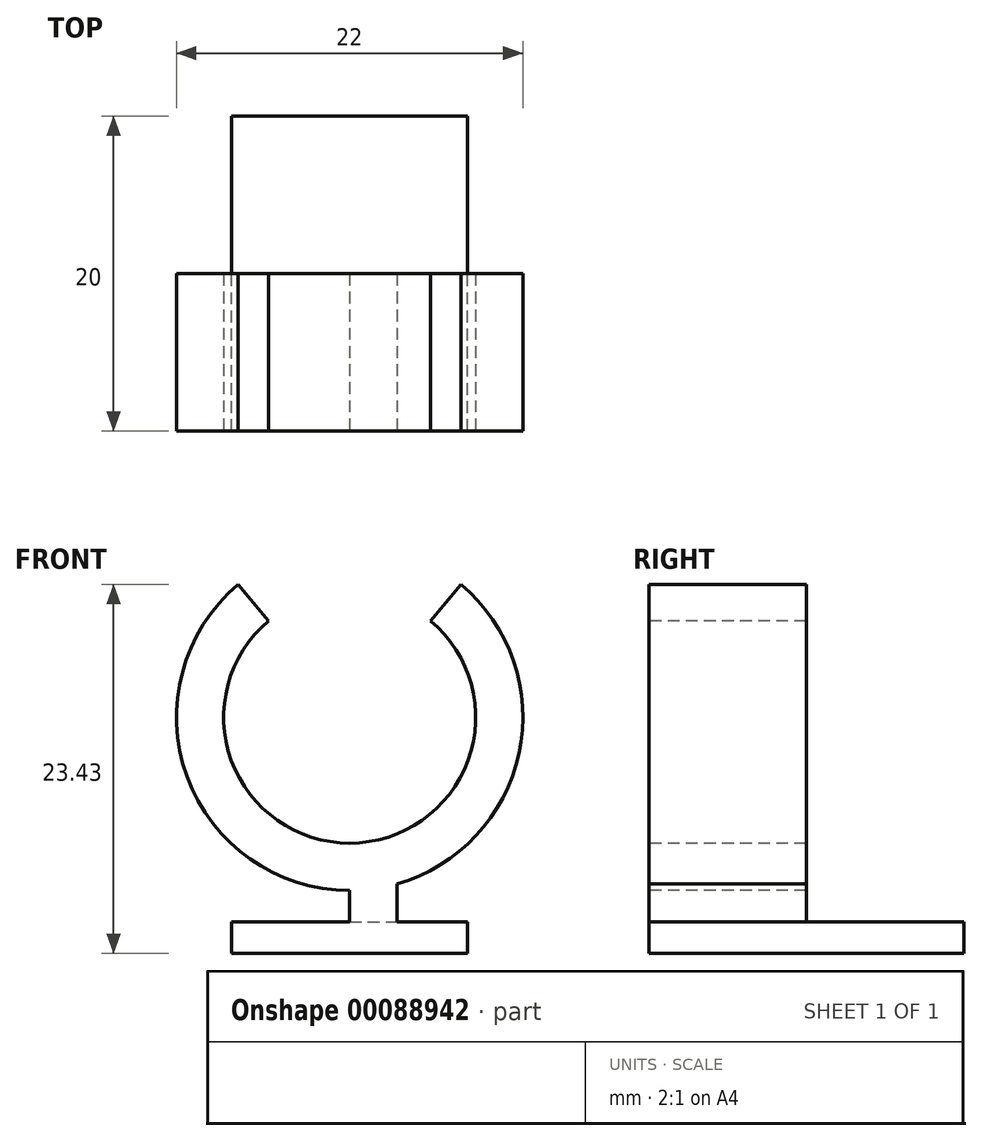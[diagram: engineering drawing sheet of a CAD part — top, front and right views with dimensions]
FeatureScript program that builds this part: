
annotation { "Feature Type Name" : "Feature", "Feature Type Description" : "" }
export const myFeature = defineFeature(function(context is Context, id is Id, definition is map)
    precondition{}
    {
        {
            var Q0;
            Q0=qCreatedBy(makeId("Top.planeOp"),FACE);
            var sketch = newSketch(context, id + "F0", { "sketchPlane" : qUnion([Q0])});
            skLineSegment(sketch, "E0.bottom", {"start": v(0, 0) * mm, "end": v(14.98, 0) * mm});
            skLineSegment(sketch, "E0.top", {"start": v(0, 20) * mm, "end": v(14.98, 20) * mm});
            skLineSegment(sketch, "E0.left", {"start": v(0, 0) * mm, "end": v(0, 20) * mm});
            skLineSegment(sketch, "E0.right", {"start": v(14.98, 0) * mm, "end": v(14.98, 20) * mm});
            skSolve(sketch);
        }
        {
            var Q0;
            Q0=makeQuery(id+"F0.imprint","IMPRINT",FACE,{"disambiguationData":[TD([[makeQuery(id+"F0.imprint","IMPRINT",EDGE,{"derivedFrom":sQuery(id+"F0.wireOp",EDGE,"E0.bottom")}),1.0]])]});
            extrude(context, id + "F1", {"entities" : qUnion([Q0]), "oppositeDirection" : true, "depth" : 2 * mm});
        }
        {
            var Q0;
            Q0=makeQuery(id+"F1.opExtrude","SWEPT_FACE",FACE,{"disambiguationData":[OSD([sQuery(id+"F0.wireOp",EDGE,"E0.bottom")])]});
            var sketch = newSketch(context, id + "F2", { "sketchPlane" : qUnion([Q0])});
            skLineSegment(sketch, "E1", {"start": v(0, 0) * mm, "end": v(7.49, 0) * mm});
            skLineSegment(sketch, "E2", {"start": v(7.49, 0) * mm, "end": v(4.49, 0) * mm});
            skLineSegment(sketch, "E3", {"start": v(4.49, 0) * mm, "end": v(4.49, 5) * mm});
            skLineSegment(sketch, "E4", {"start": v(4.49, 5) * mm, "end": v(10.49, 5) * mm});
            skLineSegment(sketch, "E5", {"start": v(10.49, 5) * mm, "end": v(10.49, 0) * mm});
            skLineSegment(sketch, "E6", {"start": v(7.49, 0) * mm, "end": v(7.49, 5) * mm});
            skLineSegment(sketch, "E7", {"start": v(7.49, 5) * mm, "end": v(7.49, 13) * mm});
            skCircle(sketch, "E8", {"center": v(7.49, 13) * mm, "radius": 8 * mm});
            skCircle(sketch, "E9", {"center": v(7.49, 13) * mm, "radius": 11 * mm});
            skLineSegment(sketch, "E10", {"start": v(7.49, 13) * mm, "end": v(-3.51, 13) * mm});
            skLineSegment(sketch, "E11", {"start": v(7.49, 13) * mm, "end": v(0.42, 21.43) * mm});
            skLineSegment(sketch, "E12", {"start": v(7.49, 13) * mm, "end": v(14.56, 21.43) * mm});
            skSolve(sketch);
        }
        {
            var Q0;
            {var subQ0=sQuery(id+"F2.wireOp",EDGE,"E5");var subQ1=makeQuery(id+"F1.opExtrude","CAP_EDGE",EDGE,{"disambiguationData":[OSD([sQuery(id+"F0.wireOp",EDGE,"E0.bottom")])],"isStart":true});var subQ2=makeQuery(id+"F2.imprint","INTERSECT",VERTEX,{"derivedFrom":[subQ1,subQ0]});Q0=makeQuery(id+"F2.imprint","IMPRINT",FACE,{"disambiguationData":[TD([[makeQuery(id+"F2.imprint","IMPRINT",EDGE,{"disambiguationData":[TD([[subQ2,1.0]])],"derivedFrom":subQ0}),-1.0]])]});}
            var Q1;
            {var subQ0=sQuery(id+"F2.wireOp",EDGE,"E2");Q1=makeQuery(id+"F2.imprint","IMPRINT",FACE,{"disambiguationData":[TD([[makeQuery(id+"F2.imprint","IMPRINT",EDGE,{"derivedFrom":subQ0}),1.0]])]});}
            var Q2;
            {var subQ0=sQuery(id+"F2.wireOp",EDGE,"E4");var subQ1=sQuery(id+"F2.wireOp",EDGE,"E3");var subQ2=makeQuery(id+"F2.imprint","INTERSECT",VERTEX,{"derivedFrom":[subQ1,subQ0]});Q2=makeQuery(id+"F2.imprint","IMPRINT",FACE,{"disambiguationData":[TD([[makeQuery(id+"F2.imprint","IMPRINT",EDGE,{"disambiguationData":[TD([[subQ2,1.0]])],"derivedFrom":subQ1}),-1.0]])]});}
            var Q3;
            {var subQ0=sQuery(id+"F2.wireOp",EDGE,"E5");var subQ1=sQuery(id+"F2.wireOp",EDGE,"E4");var subQ2=makeQuery(id+"F2.imprint","INTERSECT",VERTEX,{"derivedFrom":[subQ1,subQ0]});Q3=makeQuery(id+"F2.imprint","IMPRINT",FACE,{"disambiguationData":[TD([[makeQuery(id+"F2.imprint","IMPRINT",EDGE,{"disambiguationData":[TD([[subQ2,-1.0]])],"derivedFrom":subQ0}),-1.0]])]});}
            var Q4;
            {var subQ3=sQuery(id+"F2.wireOp",EDGE,"E5");var subQ6=sQuery(id+"F2.wireOp",EDGE,"E4");var subQ9=makeQuery(id+"F2.imprint","INTERSECT",VERTEX,{"derivedFrom":[subQ6,subQ3]});Q4=makeQuery(id+"F2.imprint","IMPRINT",FACE,{"disambiguationData":[TD([[makeQuery(id+"F2.imprint","IMPRINT",EDGE,{"disambiguationData":[TD([[subQ9,-1.0]])],"derivedFrom":subQ3}),1.0]])]});}
            var Q5;
            {var subQ3=sQuery(id+"F2.wireOp",EDGE,"E3");var subQ6=sQuery(id+"F2.wireOp",EDGE,"E4");var subQ9=makeQuery(id+"F2.imprint","INTERSECT",VERTEX,{"derivedFrom":[subQ3,subQ6]});Q5=makeQuery(id+"F2.imprint","IMPRINT",FACE,{"disambiguationData":[TD([[makeQuery(id+"F2.imprint","IMPRINT",EDGE,{"disambiguationData":[TD([[subQ9,1.0]])],"derivedFrom":subQ3}),1.0]])]});}
            var Q6;
            {var subQ0=sQuery(id+"F2.wireOp",EDGE,"E11");var subQ1=sQuery(id+"F2.wireOp",EDGE,"E8");var subQ2=makeQuery(id+"F2.imprint","INTERSECT",VERTEX,{"derivedFrom":[subQ1,subQ0]});Q6=makeQuery(id+"F2.imprint","IMPRINT",FACE,{"disambiguationData":[TD([[makeQuery(id+"F2.imprint","IMPRINT",EDGE,{"disambiguationData":[TD([[subQ2,-1.0]])],"derivedFrom":subQ1}),-1.0]])]});}
            extrude(context, id + "F3", {"entities" : qUnion([Q0, Q1, Q2, Q3, Q4, Q5, Q6]), "operationType" : NewBodyOperationType.ADD, "oppositeDirection" : true, "depth" : 10 * mm});
        }
    });
